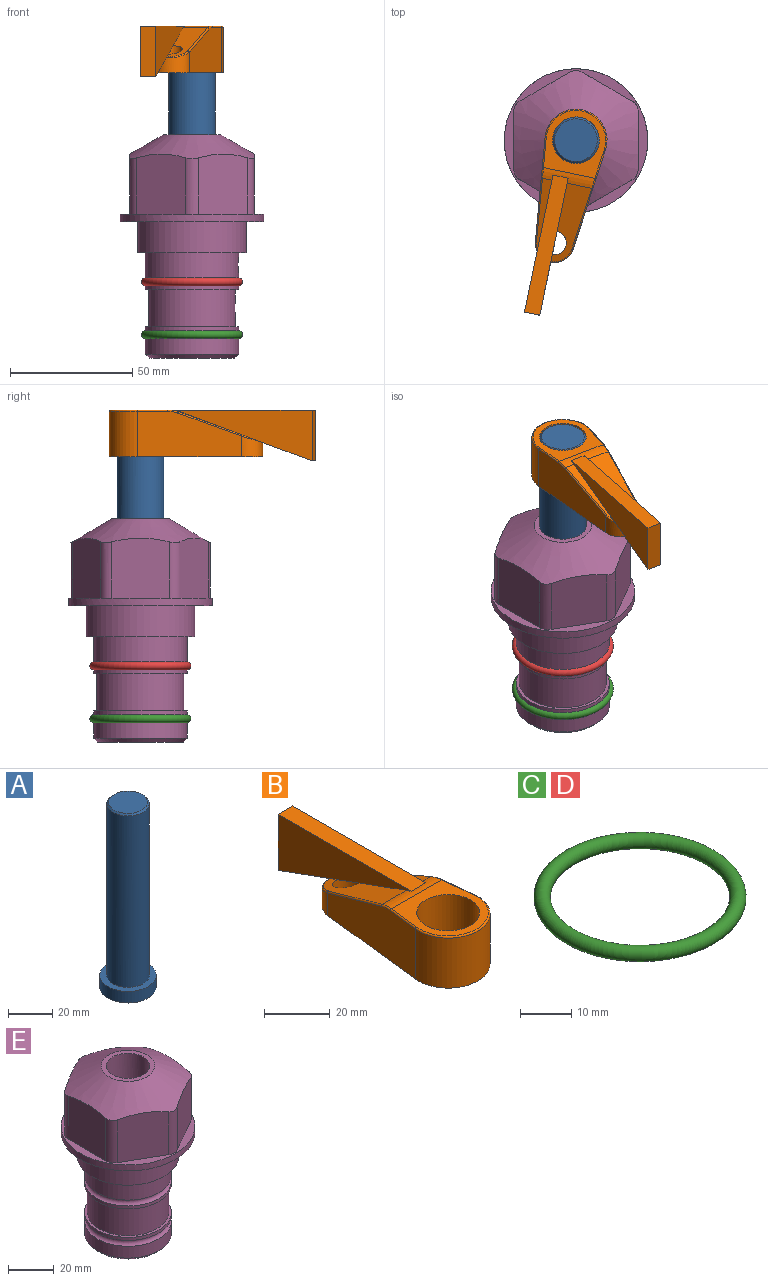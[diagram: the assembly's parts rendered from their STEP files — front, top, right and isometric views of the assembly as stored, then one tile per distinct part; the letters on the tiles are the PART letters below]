
ASSEMBLY  parts=5 mates=3
PART A: 6 faces, bbox 25.4x25.4x101.6 mm
  f0: plane 17.46x17.46mm, normal (0,0,1), area 239.5mm2, adj f5
  f1: plane 25.4x25.4mm, normal (0,0,-1), area 506.7mm2, adj f2
  f2: cylinder r=12.7mm len=25.4mm, axis (0,0,1), area 506.7mm2, adj f1,f3
  f3: plane 25.4x25.4mm, normal (0,0,1), area 221.7mm2, adj f2,f4
  f4: cylinder r=9.53mm len=94.46mm, axis (0,0,1), area 5653mm2, adj f3,f5
  f5: cone r=8.73mm half-angle=45deg, axis (0,0,-1), area 64.4mm2, adj f0,f4
PART B: 52 faces, bbox 27.5x86.7x20.8 mm
  f0: plane 28.91x10.52mm, normal (0,0.34,0.94), area 70.4mm2, adj f11,f15,f17,f50
  f1: plane 2.3x0.95mm, normal (0,0,-1), area 1mm2, adj f26,f31,f35
  f2: plane 63.5x25.4mm, normal (0,0,-1), area 561.7mm2, adj f3,f4,f5,f6,f7,f8,f20,f21
  f3: cylinder r=12.7mm len=25.4mm, axis (0,0,-1), area 792.2mm2, adj f2,f4,f6,f14
  f4: plane 42.33x18.54mm, normal (0.99,0.11,0), area 647mm2, adj f2,f3,f5,f12,f13,f15
  f5: cylinder r=7.94mm len=15.78mm, axis (0,0,-1), area 158.6mm2, adj f2,f4,f6,f17
  f6: plane 42.33x18.54mm, normal (-0.99,0.11,0), area 647mm2, adj f2,f3,f5,f16,f18,f19
  f7: cylinder r=9.53mm len=19.05mm, axis (0,0,-1), area 1140.1mm2, adj f2,f9
  f8: cylinder r=4.76mm len=10.96mm, axis (0,0,-1), area 276.1mm2, adj f2,f10,f47
  f9: plane 25.83x24.38mm, normal (0,0,1), area 262.2mm2, adj f7,f11,f12,f14,f16
  f10: plane 32.49x11.82mm, normal (0,0.34,0.94), area 244.9mm2, adj f8,f11,f17,f19,f51
  f11: cylinder r=12.7mm len=21.49mm, axis (-1,0,0), area 93.2mm2, adj f0,f9,f10,f13,f18,f46
  f12: cylinder r=0.51mm len=12.34mm, axis (0.11,-0.99,0), area 9.9mm2, adj f4,f9,f13,f14
  f13: bspline ~7.62x1.64mm, area 3.5mm2, adj f4,f11,f12,f15
  f14: torus R=12.19mm, axis (0,0,1), area 33.6mm2, adj f3,f9,f12,f16
  f15: cylinder r=0.51mm len=26.01mm, axis (0.1,-0.93,0.34), area 21.6mm2, adj f0,f4,f13,f17
  f16: cylinder r=0.51mm len=12.34mm, axis (0.11,0.99,0), area 9.9mm2, adj f6,f9,f14,f18
  f17: bspline ~15.78x7.05mm, area 15.7mm2, adj f0,f5,f10,f15,f19,f45
  f18: bspline ~7.62x1.64mm, area 3.5mm2, adj f6,f11,f16,f19
  f19: cylinder r=0.51mm len=26.01mm, axis (0.1,0.93,-0.34), area 21.6mm2, adj f6,f10,f17,f18
  f20: plane 21.6x14.29mm, normal (-0.99,-0.11,0), area 242.6mm2, adj f2,f27,f29,f35,f37,f39
  f21: plane 21.6x14.29mm, normal (0.99,-0.11,0), area 242.6mm2, adj f2,f28,f30,f38,f40,f42
  f22: cylinder r=12.7mm len=14.29mm, axis (0,0,-1), area 173.2mm2, adj f2,f27,f28,f31,f32,f34
  f23: cylinder r=7.94mm len=7.63mm, axis (0,0,-1), area 53.8mm2, adj f2,f29,f30,f43
  f24: plane 2.3x0.95mm, normal (0,0,-1), area 1mm2, adj f26,f34,f38
  f25: plane 17.94x12.32mm, normal (0,-0.34,-0.94), area 191.2mm2, adj f26,f39,f42,f43
  f26: cylinder r=9.53mm len=12.93mm, axis (-1,0,0), area 37.5mm2, adj f1,f24,f25,f32,f37,f40
  f27: cylinder r=1.59mm len=14.29mm, axis (0,0,-1), area 49mm2, adj f2,f20,f22,f33
  f28: cylinder r=1.59mm len=14.29mm, axis (0,0,-1), area 49mm2, adj f2,f21,f22,f36
  f29: cylinder r=1.59mm len=7.28mm, axis (0,0,-1), area 22.1mm2, adj f2,f20,f23,f41
  f30: cylinder r=1.59mm len=7.28mm, axis (0,0,-1), area 22.1mm2, adj f2,f21,f23,f44
  f31: torus R=14.29mm, axis (0,0,1), area 5.8mm2, adj f1,f22,f32,f33
  f32: bspline ~11.06x2.73mm, area 20.8mm2, adj f22,f26,f31,f34
  f33: sphere r=1.59mm, area 5.4mm2, adj f27,f31,f35
  f34: torus R=14.29mm, axis (0,0,1), area 5.8mm2, adj f22,f24,f32,f36
  f35: cylinder r=1.59mm len=1.68mm, axis (-0.11,0.99,0), area 2.4mm2, adj f1,f20,f33,f37
  f36: sphere r=1.59mm, area 5.4mm2, adj f28,f34,f38
  f37: bspline ~5.82x2.33mm, area 7.7mm2, adj f20,f26,f35,f39
  f38: cylinder r=1.59mm len=1.68mm, axis (0.11,0.99,0), area 2.4mm2, adj f21,f24,f36,f40
  f39: cylinder r=1.59mm len=18.33mm, axis (0.1,-0.93,0.34), area 46.7mm2, adj f20,f25,f37,f41
  f40: bspline ~5.82x2.33mm, area 7.7mm2, adj f21,f26,f38,f42
  f41: sphere r=1.59mm, area 3.6mm2, adj f29,f39,f43
  f42: cylinder r=1.59mm len=18.33mm, axis (0.1,0.93,-0.34), area 46.7mm2, adj f21,f25,f40,f44
  f43: bspline ~8.31x1.84mm, area 15.3mm2, adj f23,f25,f41,f44
  f44: sphere r=1.59mm, area 3.6mm2, adj f30,f42,f43
  f45: plane 26.11x9.5mm, normal (0,-0.34,-0.94), area 159.3mm2, adj f17,f48,f50,f51
  f46: plane 6.35x2.1mm, normal (0,-0.34,-0.94), area 14.2mm2, adj f11,f49,f50,f51
  f47: plane 9.53x4.76mm, normal (0,-0.34,-0.94), area 37.9mm2, adj f8,f51
  f48: plane 20.79x6.35mm, normal (0,1,0), area 132mm2, adj f45,f49,f50,f51
  f49: plane 57.12x6.35mm, normal (0,0,1), area 362.7mm2, adj f46,f48,f50,f51
  f50: plane 57.12x20.79mm, normal (1,0,0), area 593.8mm2, adj f0,f45,f46,f48,f49
  f51: plane 57.12x20.79mm, normal (-1,0,0), area 593.8mm2, adj f10,f45,f46,f47,f48,f49
PART C: 1 faces, bbox 44.7x44.7x3.2 mm
  f0: torus R=19.05mm, axis (0,0,1), area 1193.9mm2
PART D: same geometry as C
PART E: 36 faces, bbox 58.7x58.7x91.2 mm
  f0: cylinder r=17.78mm len=35.56mm, axis (0,0,1), area 1670.8mm2, adj f23,f24,f31
  f1: cylinder r=19.05mm len=38.1mm, axis (0,0,1), area 1191.9mm2, adj f26,f27,f30
  f2: plane 58.66x58.66mm, normal (0,0,-1), area 1150.6mm2, adj f3,f28
  f3: cylinder r=29.33mm len=58.66mm, axis (0,0,-1), area 585.1mm2, adj f2,f4
  f4: plane 58.66x58.66mm, normal (0,0,1), area 475.9mm2, adj f3,f5,f6,f7,f8,f9,f10,f11
  f5: plane 24.5x20.32mm, normal (-0.5,0.87,0), area 562.8mm2, adj f4,f15,f16,f17
  f6: plane 24.5x20.32mm, normal (0.5,0.87,0), area 562.8mm2, adj f4,f14,f15,f17
  f7: plane 24.5x23.48mm, normal (1,0,0), area 562.8mm2, adj f4,f13,f14,f17
  f8: plane 24.5x20.32mm, normal (0.5,-0.87,0), area 562.8mm2, adj f4,f12,f13,f17
  f9: plane 24.5x20.32mm, normal (-0.5,-0.87,0), area 562.8mm2, adj f4,f11,f12,f17
  f10: plane 24.5x23.48mm, normal (-1,0,0), area 562.8mm2, adj f4,f11,f16,f17
  f11: cylinder r=5.08mm len=23.01mm, axis (0,0,-1), area 121.2mm2, adj f4,f9,f10,f17
  f12: cylinder r=5.08mm len=23.01mm, axis (0,0,-1), area 121.2mm2, adj f4,f8,f9,f17
  f13: cylinder r=5.08mm len=23.01mm, axis (0,0,-1), area 121.2mm2, adj f4,f7,f8,f17
  f14: cylinder r=5.08mm len=23.01mm, axis (0,0,-1), area 121.2mm2, adj f4,f6,f7,f17
  f15: cylinder r=5.08mm len=23.01mm, axis (0,0,-1), area 121.2mm2, adj f4,f5,f6,f17
  f16: cylinder r=5.08mm len=23.01mm, axis (0,0,-1), area 121.2mm2, adj f4,f5,f10,f17
  f17: cone r=11.73mm half-angle=60deg, axis (0,0,-1), area 2071.8mm2, adj f5,f6,f7,f8,f9,f10,f11,f12
  f18: plane 23.46x23.46mm, normal (0,0,1), area 147.4mm2, adj f17,f35
  f19: plane 34.93x34.93mm, normal (0,0,-1), area 958mm2, adj f29
  f20: cylinder r=19.05mm len=38.1mm, axis (0,0,1), area 760.1mm2, adj f21,f29
  f21: torus R=19.05mm, axis (0,0,1), area 565.3mm2, adj f20,f22
  f22: cylinder r=19.05mm len=38.1mm, axis (0,0,1), area 190mm2, adj f21,f23
  f23: plane 38.1x38.1mm, normal (0,0,1), area 146.9mm2, adj f0,f22
  f24: plane 38.1x38.1mm, normal (0,0,-1), area 146.9mm2, adj f0,f25
  f25: cylinder r=19.05mm len=38.1mm, axis (0,0,1), area 190mm2, adj f24,f26
  f26: torus R=19.05mm, axis (0,0,1), area 565.3mm2, adj f1,f25
  f27: plane 44.45x44.45mm, normal (0,0,-1), area 411.7mm2, adj f1,f28
  f28: cylinder r=22.23mm len=44.45mm, axis (0,0,1), area 1773.5mm2, adj f2,f27
  f29: cone r=19.05mm half-angle=45deg, axis (0,0,1), area 257.5mm2, adj f19,f20
  f30: cylinder r=3.17mm len=6.75mm, axis (-1,0,0), area 128mm2, adj f1,f33
  f31: cylinder r=3.17mm len=6.35mm, axis (-1,0,0), area 102.5mm2, adj f0,f33
  f32: plane 25.4x25.4mm, normal (0,0,1), area 506.7mm2, adj f33
  f33: cylinder r=12.7mm len=66.42mm, axis (0,0,-1), area 5236.2mm2, adj f30,f31,f32,f34
  f34: cone r=9.53mm half-angle=30deg, axis (0,0,-1), area 443.4mm2, adj f33,f35
  f35: cylinder r=9.53mm len=19.05mm, axis (0,0,-1), area 849mm2, adj f18,f34
PLACE A rot(axis=(0,0,-1),101.7deg) t=(0,0,6.38)mm
PLACE B rot(axis=(0,0,1),168.3deg) t=(0,0,60.99)mm
PLACE C t=(0,0,-21.59)mm
PLACE D at identity
PLACE E at identity fixed
MATE fastened C.f0 <-> E.f0  axis (0,0,1) through (0,0,-46.1)mm
MATE cylindrical A.f2 <-> E.f0  axis (0,0,1) through (0,0,32.01)mm
MATE fastened B.f3 <-> A.f2  axis (0,0,1) through (0,0,80.04)mm
